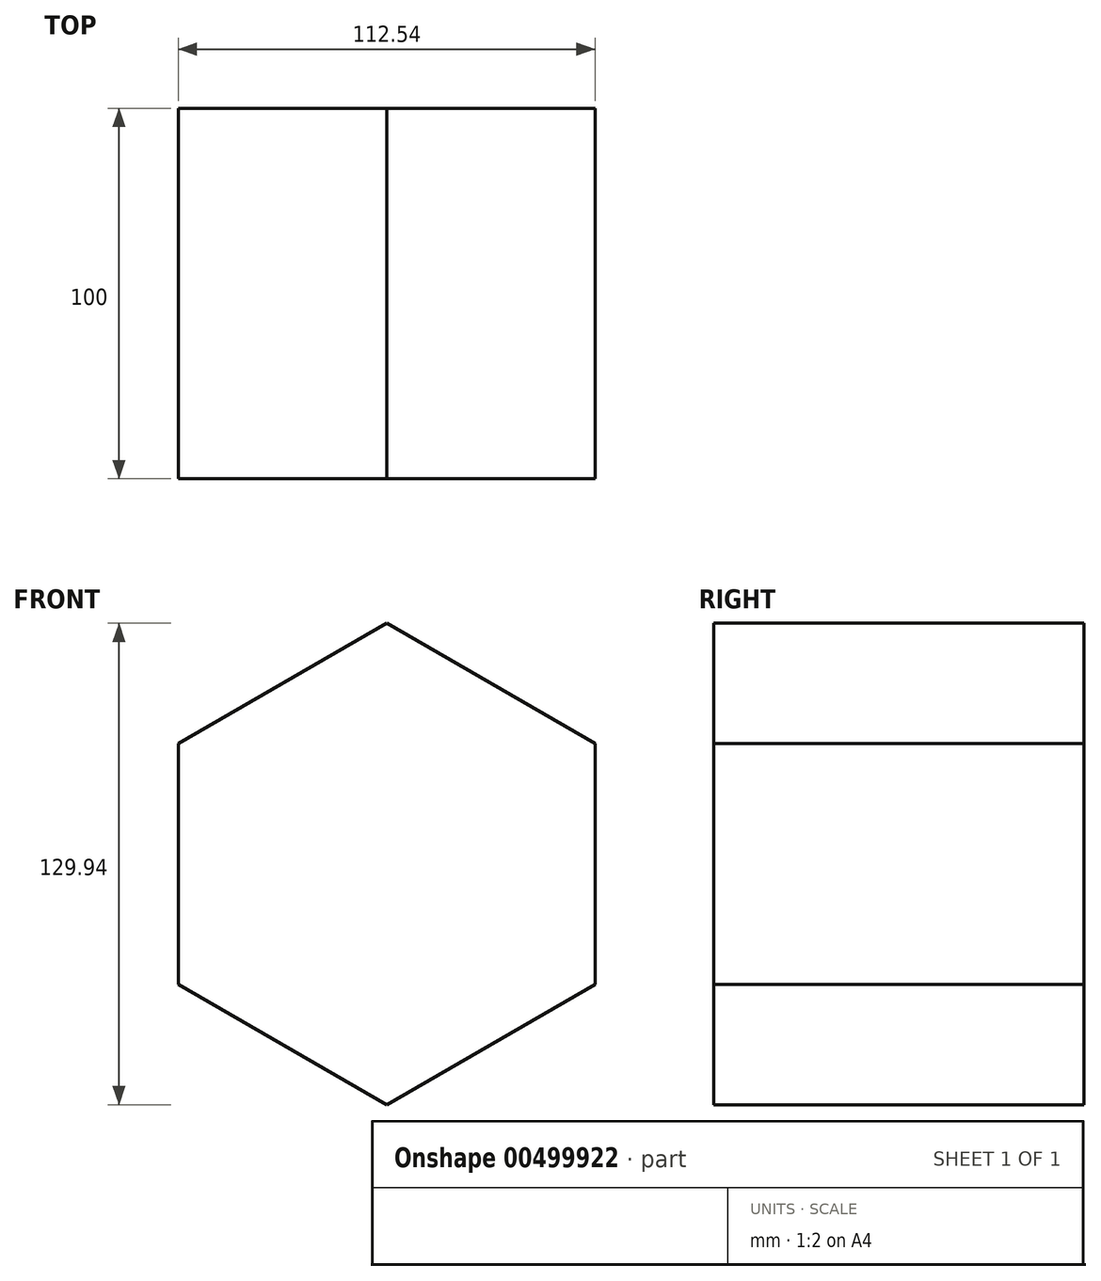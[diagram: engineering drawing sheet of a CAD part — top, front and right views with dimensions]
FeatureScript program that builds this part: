
annotation { "Feature Type Name" : "Feature", "Feature Type Description" : "" }
export const myFeature = defineFeature(function(context is Context, id is Id, definition is map)
    precondition{}
    {
        {
            var Q0;
            Q0=qCreatedBy(makeId("Front.planeOp"),FACE);
            var sketch = newSketch(context, id + "F0", { "sketchPlane" : qUnion([Q0])});
            skCircle(sketch, "E0.cCircle", {"center": v(0, 0) * mm, "radius": 64.97 * mm, "construction": true});
            skLineSegment(sketch, "E0.0", {"start": v(56.25, 32.5) * mm, "end": v(56.27, -32.47) * mm});
            skLineSegment(sketch, "E0.1", {"start": v(56.27, -32.47) * mm, "end": v(0.02, -64.97) * mm});
            skLineSegment(sketch, "E0.2", {"start": v(0.02, -64.97) * mm, "end": v(-56.25, -32.5) * mm});
            skLineSegment(sketch, "E0.3", {"start": v(-56.25, -32.5) * mm, "end": v(-56.27, 32.47) * mm});
            skLineSegment(sketch, "E0.4", {"start": v(-56.27, 32.47) * mm, "end": v(-0.02, 64.97) * mm});
            skLineSegment(sketch, "E0.5", {"start": v(-0.02, 64.97) * mm, "end": v(56.25, 32.5) * mm});
            skSolve(sketch);
        }
        {
            var Q0;
            Q0=makeQuery(id+"F0.imprint","IMPRINT",FACE,{"disambiguationData":[TD([[makeQuery(id+"F0.imprint","IMPRINT",EDGE,{"derivedFrom":sQuery(id+"F0.wireOp",EDGE,"E0.0")}),-1.0]])]});
            extrude(context, id + "F1", {"entities" : qUnion([Q0]), "depth" : 100 * mm, "symmetric" : true});
        }
    });
